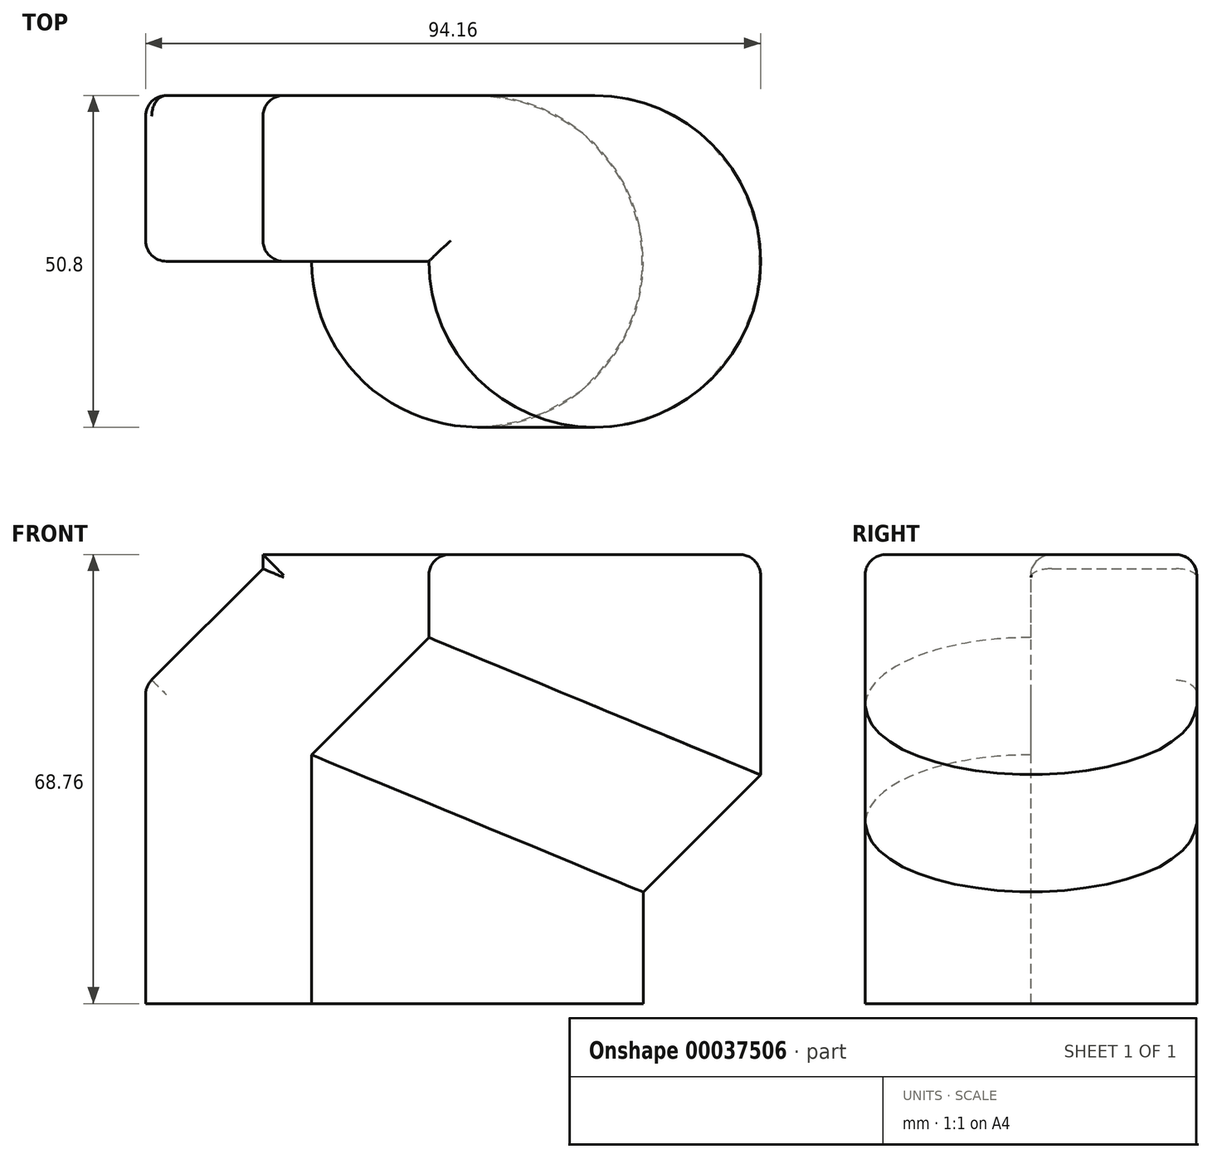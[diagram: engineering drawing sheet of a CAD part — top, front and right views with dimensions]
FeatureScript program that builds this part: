
annotation { "Feature Type Name" : "Feature", "Feature Type Description" : "" }
export const myFeature = defineFeature(function(context is Context, id is Id, definition is map)
    precondition{}
    {
        {
            var Q0;
            Q0=qCreatedBy(makeId("Top.planeOp"),FACE);
            var sketch = newSketch(context, id + "F0", { "sketchPlane" : qUnion([Q0])});
            skLineSegment(sketch, "E0.bottom", {"start": v(0, 0) * mm, "end": v(50.8, 0) * mm});
            skLineSegment(sketch, "E0.top", {"start": v(0, -25.4) * mm, "end": v(25.4, -25.4) * mm});
            skLineSegment(sketch, "E0.left", {"start": v(0, 0) * mm, "end": v(0, -25.4) * mm});
            skArc(sketch, "E1", {"start": v(25.4, -25.4) * mm, "mid": v(68.76, -43.36) * mm, "end": v(50.8, 0) * mm});
            skSolve(sketch);
        }
        {
            var Q0;
            Q0=qCreatedBy(makeId("Front.planeOp"),FACE);
            var sketch = newSketch(context, id + "F1", { "sketchPlane" : qUnion([Q0])});
            skLineSegment(sketch, "E2", {"start": v(25.4, 0) * mm, "end": v(25.4, 38.1) * mm});
            skLineSegment(sketch, "E3", {"start": v(25.4, 38.1) * mm, "end": v(43.36, 56.06) * mm});
            skLineSegment(sketch, "E4", {"start": v(43.36, 56.06) * mm, "end": v(43.36, 68.76) * mm});
            skSolve(sketch);
        }
        {
            var Q0;
            Q0=makeQuery(id+"F0.imprint","IMPRINT",FACE,{"disambiguationData":[TD([[makeQuery(id+"F0.imprint","IMPRINT",EDGE,{"derivedFrom":sQuery(id+"F0.wireOp",EDGE,"E0.bottom")}),-1.0]])]});
            var Q1;
            Q1=sQuery(id+"F1.wireOp",EDGE,"E2");
            var Q2;
            Q2=sQuery(id+"F1.wireOp",EDGE,"E3");
            var Q3;
            Q3=sQuery(id+"F1.wireOp",EDGE,"E4");
            sweep(context, id + "F2", {"profiles" : qUnion([Q0]), "path" : qUnion([Q1, Q2, Q3])});
        }
        {
            var Q0;
            Q0=makeQuery(id+"F2.opSweep","SWEPT_EDGE",EDGE,{"disambiguationData":[OSD([sQuery(id+"F0.wireOp",EDGE,"E0.top"),sQuery(id+"F0.wireOp",EDGE,"E0.left"),sQuery(id+"F1.wireOp",EDGE,"E3")])]});
            var Q1;
            Q1=makeQuery(id+"F2.opSweep","SWEPT_EDGE",EDGE,{"disambiguationData":[OSD([sQuery(id+"F0.wireOp",EDGE,"E0.top"),sQuery(id+"F0.wireOp",EDGE,"E0.left"),sQuery(id+"F1.wireOp",EDGE,"E2")])]});
            var Q2;
            Q2=makeQuery(id+"F2.opSweep","MID_CAP_EDGE",EDGE,{"disambiguationData":[OSD([sQuery(id+"F0.wireOp",EDGE,"E0.left"),sQuery(id+"F1.wireOp",VERTEX,"E3.start")])],"capPos":1.0});
            var Q3;
            Q3=makeQuery(id+"F2.opSweep","SWEPT_EDGE",EDGE,{"disambiguationData":[OSD([sQuery(id+"F0.wireOp",EDGE,"E0.bottom"),sQuery(id+"F0.wireOp",EDGE,"E0.left"),sQuery(id+"F1.wireOp",EDGE,"E2")])]});
            var Q4;
            Q4=makeQuery(id+"F2.opSweep","SWEPT_EDGE",EDGE,{"disambiguationData":[OSD([sQuery(id+"F0.wireOp",EDGE,"E0.bottom"),sQuery(id+"F0.wireOp",EDGE,"E0.left"),sQuery(id+"F1.wireOp",EDGE,"E3")])]});
            var Q5;
            Q5=makeQuery(id+"F2.opSweep","SWEPT_EDGE",EDGE,{"disambiguationData":[OSD([sQuery(id+"F0.wireOp",EDGE,"E0.top"),sQuery(id+"F0.wireOp",EDGE,"E0.left"),sQuery(id+"F1.wireOp",EDGE,"E4")])]});
            var Q6;
            Q6=makeQuery(id+"F2.opSweep","CAP_EDGE",EDGE,{"disambiguationData":[OSD([sQuery(id+"F0.wireOp",EDGE,"E0.top"),sQuery(id+"F1.wireOp",VERTEX,"E4.end")])],"isStart":false});
            var Q7;
            Q7=makeQuery(id+"F2.opSweep","SWEPT_EDGE",EDGE,{"disambiguationData":[OSD([sQuery(id+"F0.wireOp",EDGE,"E0.bottom"),sQuery(id+"F0.wireOp",EDGE,"E0.left"),sQuery(id+"F1.wireOp",EDGE,"E4")])]});
            var Q8;
            Q8=makeQuery(id+"F2.opSweep","CAP_EDGE",EDGE,{"disambiguationData":[OSD([sQuery(id+"F0.wireOp",EDGE,"E0.bottom"),sQuery(id+"F1.wireOp",VERTEX,"E4.end")])],"isStart":false});
            fillet(context, id + "F3", {"entities" : qUnion([Q0, Q1, Q2, Q3, Q4, Q5, Q6, Q7, Q8]), "radius" : 3.17 * mm, "tangentPropagation" : true, "allowEdgeOverflow" : false});
        }
    });
